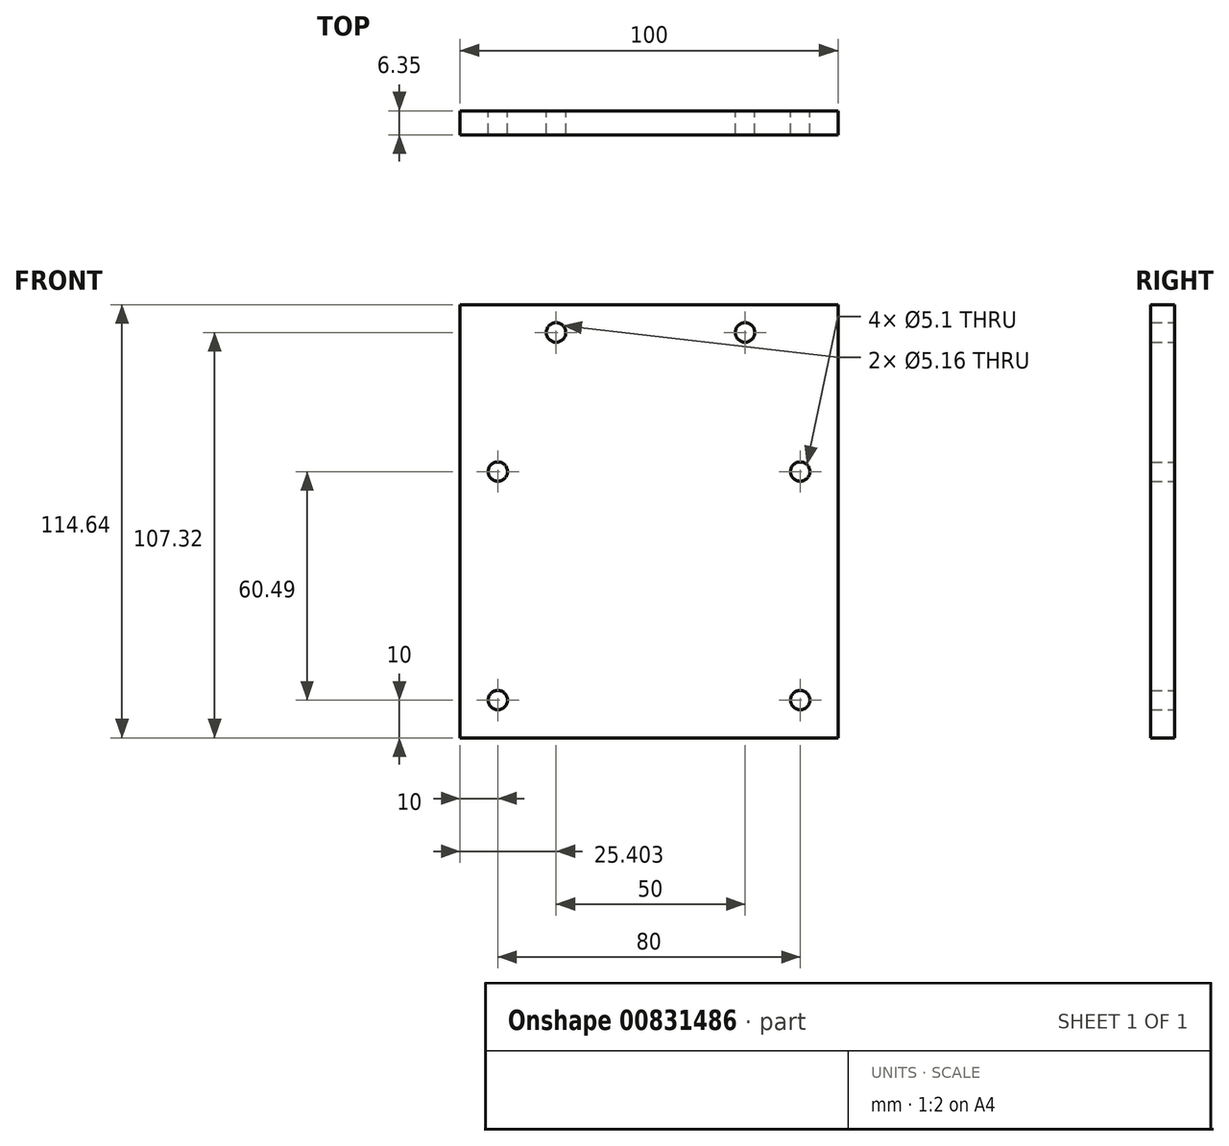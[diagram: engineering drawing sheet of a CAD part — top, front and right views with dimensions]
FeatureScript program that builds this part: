
annotation { "Feature Type Name" : "Feature", "Feature Type Description" : "" }
export const myFeature = defineFeature(function(context is Context, id is Id, definition is map)
    precondition{}
    {
        {
            var Q0;
            Q0=qCreatedBy(makeId("Front.planeOp"),FACE);
            var sketch = newSketch(context, id + "F0", { "sketchPlane" : qUnion([Q0])});
            skLineSegment(sketch, "E0.top", {"start": v(50, -50) * mm, "end": v(-50, -50) * mm});
            skLineSegment(sketch, "E0.left", {"start": v(50, 50) * mm, "end": v(50, -50) * mm});
            skLineSegment(sketch, "E0.right", {"start": v(-50, 50) * mm, "end": v(-50, -50) * mm});
            skPoint(sketch, "E0.middle", {"position": v(0, 0) * mm});
            skCircle(sketch, "E1", {"center": v(-40, 20.49) * mm, "radius": 2.55 * mm});
            skCircle(sketch, "E2", {"center": v(40, 20.49) * mm, "radius": 2.55 * mm});
            skCircle(sketch, "E3", {"center": v(40, -40) * mm, "radius": 2.55 * mm});
            skCircle(sketch, "E4", {"center": v(-40, -40) * mm, "radius": 2.55 * mm});
            skLineSegment(sketch, "E5", {"start": v(-50, 50) * mm, "end": v(-50, 64.64) * mm});
            skLineSegment(sketch, "E6", {"start": v(-50, 64.64) * mm, "end": v(50, 64.64) * mm});
            skLineSegment(sketch, "E7", {"start": v(50, 64.64) * mm, "end": v(50, 50) * mm});
            skCircle(sketch, "E8", {"center": v(-24.6, 57.32) * mm, "radius": 2.58 * mm});
            skCircle(sketch, "E9", {"center": v(25.4, 57.32) * mm, "radius": 2.58 * mm});
            skSolve(sketch);
        }
        {
            var Q0;
            Q0=makeQuery(id+"F0.imprint","IMPRINT",FACE,{"disambiguationData":[TD([[makeQuery(id+"F0.imprint","IMPRINT",EDGE,{"derivedFrom":sQuery(id+"F0.wireOp",EDGE,"E0.bottom")}),1.0]])]});
            var Q1;
            Q1=makeQuery(id+"F0.imprint","IMPRINT",FACE,{"disambiguationData":[TD([[makeQuery(id+"F0.imprint","IMPRINT",EDGE,{"derivedFrom":sQuery(id+"F0.wireOp",EDGE,"E0.bottom")}),-1.0]])]});
            var Q2;
            Q2=makeQuery(id+"F0.imprint","IMPRINT",FACE,{"disambiguationData":[TD([[makeQuery(id+"F0.imprint","IMPRINT",EDGE,{"derivedFrom":sQuery(id+"F0.wireOp",EDGE,"E0.top")}),-1.0]])]});
            extrude(context, id + "F1", {"entities" : qUnion([Q0, Q1, Q2]), "depth" : 6.35 * mm, "offsetDistance" : 25 * mm});
        }
    });
